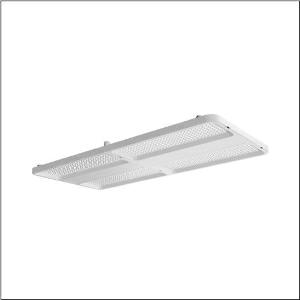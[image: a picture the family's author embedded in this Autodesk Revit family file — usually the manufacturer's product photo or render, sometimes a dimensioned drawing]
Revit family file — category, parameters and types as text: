
# Revit family: highbay_11_maxi_51hn12db4mba
name_source: partatom
category: Lighting Fixtures
units: mm (PartAtom-declared; Revit-internal decimal feet)

## family parameters
Cut with Voids When Loaded = No
Host = Face
Light Source = No
Part Type = Normal
Room Calculation Point = No
Round Connector Dimension = Use Diameter
Shared = No

## types (1)
- --- (1 x LED, 4620 lm, 22.4 W, 4000K)
    Apparent Load = 22 VA
    CIE Flux Codes = 87 98 100 100 100
    Color Rendering = 80
    Color Temperature = 4000K
    Default Elevation = 1800 mm
    Description = high bay luminaire Highbay 11 maxi; direct symmetric wide distribution, light control with lens of PMMA; UGR ≤ 22 (X = 4H | Y = 8H | S = 0.25H | reflection values 70/50/20); luminous flux: 30.000lm; light colour: 840, colour temperature: 4000K, MacAdam ≤ 2 SDCM (initial), colour rendering: CRI > 80; luminous efficacy: 204,8lm/W; rated service life: 100.000h (L95) at AT= 25°C; control: DALI 2; luminaire connection: terminal, 5-pole, max. 2.5mm² (cable entry for one cable, Ø 8.5..16mm); mains connection: 230..240V, AC/DC 0/50..60Hz; connected load: 146,5W; protection rating (complete): IP40; insulation class (complete): insulation class I (protective earthing); protection symbol: D; impact resistance: IK08; certification: CE, ENEC, VDE, UKCA; luminaire for central battery installations according to EN 60598-2-22, internal wiring halogen-free; luminaire corresponds to IFS (International Featured Standards) requirements for safety and quality in the food industry; LABS conformity tested according to VDMA 24364:2018-05; ball impact resistant only with use of appropriate mounting accessories; Suitable for use in the food industry according to the specifications of IFS-Food, HACCP and/or BRC; housing frame of high-performance plastic PA6, matt traffic white (RAL 9016); cover of PMMA; dimension (LxWxH): 946 x 442 x 72mm; permissible operating ambient temperature: -40..+60°C (reducing of maximum allowable ambient temperature of 5°C with ceiling mounting); packaging unit: 1 piece; (delivery without accessories; please order mounting accessories separately)
    Height = 72 mm  [stored 0.23622 ft]
    Lamp = 1 x LED
    Lamp Light Flux = 4620 lm
    Lamp Power = 22.4 W
    Lamp count = 1
    Length = 946 mm
    Luminous efficacy = 206 lm/W
    Manufacturer = Siteco
    ModVariant = No
    Model = 51HN12DB4MBA
    Mounting Place = Ceiling
    Mounting Type = Pendant
    Number of Poles = 1
    OnlyDefault = Yes
    Power Factor = 1
    Product Name = Highbay 11 maxi
    Product group = high bay luminaire
    ProductGroupID = 902
    Protection Class = Protection class I
    Protection Degree = IP 40
    RLX_Detail_Level = 1
    RLX_Emergency_Light_Flux = 0 lm
    RLX_Emergency_Type = 0
    RLX_Emergency_Type_DB = No
    RlxData = <blob elided: 127209 chars, md5=eda2badd>
    Socket = socket
    Standby Power = 0 W
    System Light Flux = 4620 lm
    System Power = 22 W
    Type Comments = : DC mode (central or group accumulator) initial emergency light level
    Type Image = l_1376023.jpg
    URL = http://relux.com
    VarID = @adj_016325
    Voltage = 0 V
    Weight = 0.00 kg
    Width = 442 mm

note: [stored X ft] marks values corroborated as IEEE doubles in the binary element streams (Revit-internal decimal feet)

## geometry (parser evidence)
native form markers: Blend x4, Sweep x13
no freeform markers — native parametric forms only
